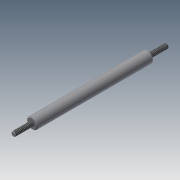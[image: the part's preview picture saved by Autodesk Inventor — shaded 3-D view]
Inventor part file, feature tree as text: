
AUTODESK INVENTOR PART (.ipt)
format: ipt  version: 2015 (Build 190159000, 159)  size: 98,816 bytes
history: native  units: mm
features: sketch x6, extrude x3, chamfer x3, hole x2, thread x2
ambient origin geometry x8: Origin, YZ Plane, XZ Plane, XY Plane, X Axis, Y Axis, Z Axis, Center Point
bodies: Solid1 (feature_tree)
feature tree (16):
  extrude  "Extrusion1"  Depth=62.7mm TaperAngle=0.0deg
  hole  "Hole1"  [1 undecoded]
  hole  "Hole2"  [1 undecoded]
  chamfer  "Chamfer1"  Distance=10.0mm
  extrude  "Extrusion2"  Depth=10.0mm TaperAngle=0.0deg
  extrude  "Extrusion3"  [1 undecoded]
  sketch  "Sketch6"  dims[d31=0.3mm d32=2.0mm d33=45.0deg]
  thread  "Thread1"  [1 undecoded]
  chamfer  "Chamfer2"  [1 undecoded]
  thread  "Thread2"  [1 undecoded]
  chamfer  "Chamfer3"  [1 undecoded]
  sketch  "Sketch1"  dims[d0=6.0mm d1=62.7mm d2=0.0mm]
  sketch  "Sketch2"  dims[d3=2.459mm d4=6.0mm d5=4.0mm d6=2.0mm d7=90.0deg d8=8.0mm d9=0.0mm]
  sketch  "Sketch3"  dims[d10=2.459mm d11=6.0mm d12=4.0mm d13=2.0mm d14=90.0deg d15=8.0mm d16=0.0mm d17=0.5mm d18=2.0mm d19=45.0deg]
  sketch  "Sketch4"  dims[d20=10.0mm d21=0.0mm d22=10.0mm d23=0.0mm d24=10.0mm d25=0.0mm]
  sketch  "Sketch5"  dims[d26=0.3mm d27=2.0mm d28=45.0deg d29=10.0mm d30=0.0mm]
note: 7 required parameter values undecoded (feature->parameter linkage not recoverable at this tier; creation-order binding heuristic only, values carry confidence <= 0.55)
